# Revit family: Lighting - Luminii - Stenos - Surface Track Master Assembly
name_source: partatom
category: Lighting Fixtures
units: mm (PartAtom-declared; Revit-internal decimal feet)

## family parameters
Cut with Voids When Loaded = No
Host = Face
Light Source = No
OmniClass Number = 23.80.70.11.14.21
OmniClass Title = Spots and Tracklight Specialties
Part Type = Normal
Room Calculation Point = No
Round Connector Dimension = Use Diameter
Shared = Yes

## types (3) — shared parameters
Apparent Load = 4 VA
Assembly Code = D5020230
Current Amps = 50 A
Default Elevation = 0"
Depth = 1 3/32"
Description = Trim Track System
Environment = Indoor
Finish = Metal - Luminii - Silver Anodized Aluminum
Frequency = 60 Hz
Instruction Sheet Link = https://www.luminii.com
Keynote = 26 50 00
Lamp = LED
Load Classification = Lighting
Manufacturer = Luminii
Number of Poles = 1
Phase = 1
Power Factor = 1
Power Source Type = Driver
Product Documentation Link = https://www.luminii.com
Product Name = Stenos Surface
Product Page URL = https://www.luminii.com
URL = https://www.luminii.com
Version = 2020 - v1.0a
Voltage = 24 V
Voltage Comments = 24 VDC
Warranty URL = https://www.luminii.com
Wattage Comments = 96 W Max per Track
Width = 15/16"

## per-type parameters (varying)
| type | Constraints | Length | Model |
| Stenos Surface - 48" | 1 | 48" | STS-48 |
| Stenos Surface - 96" | 2 | 96" | STS-96 |
| Stenos Surface - 144" | 3 | 144" | STS-144 |

## geometry (parser evidence)
native form markers: Sweep x9
no freeform markers — native parametric forms only
